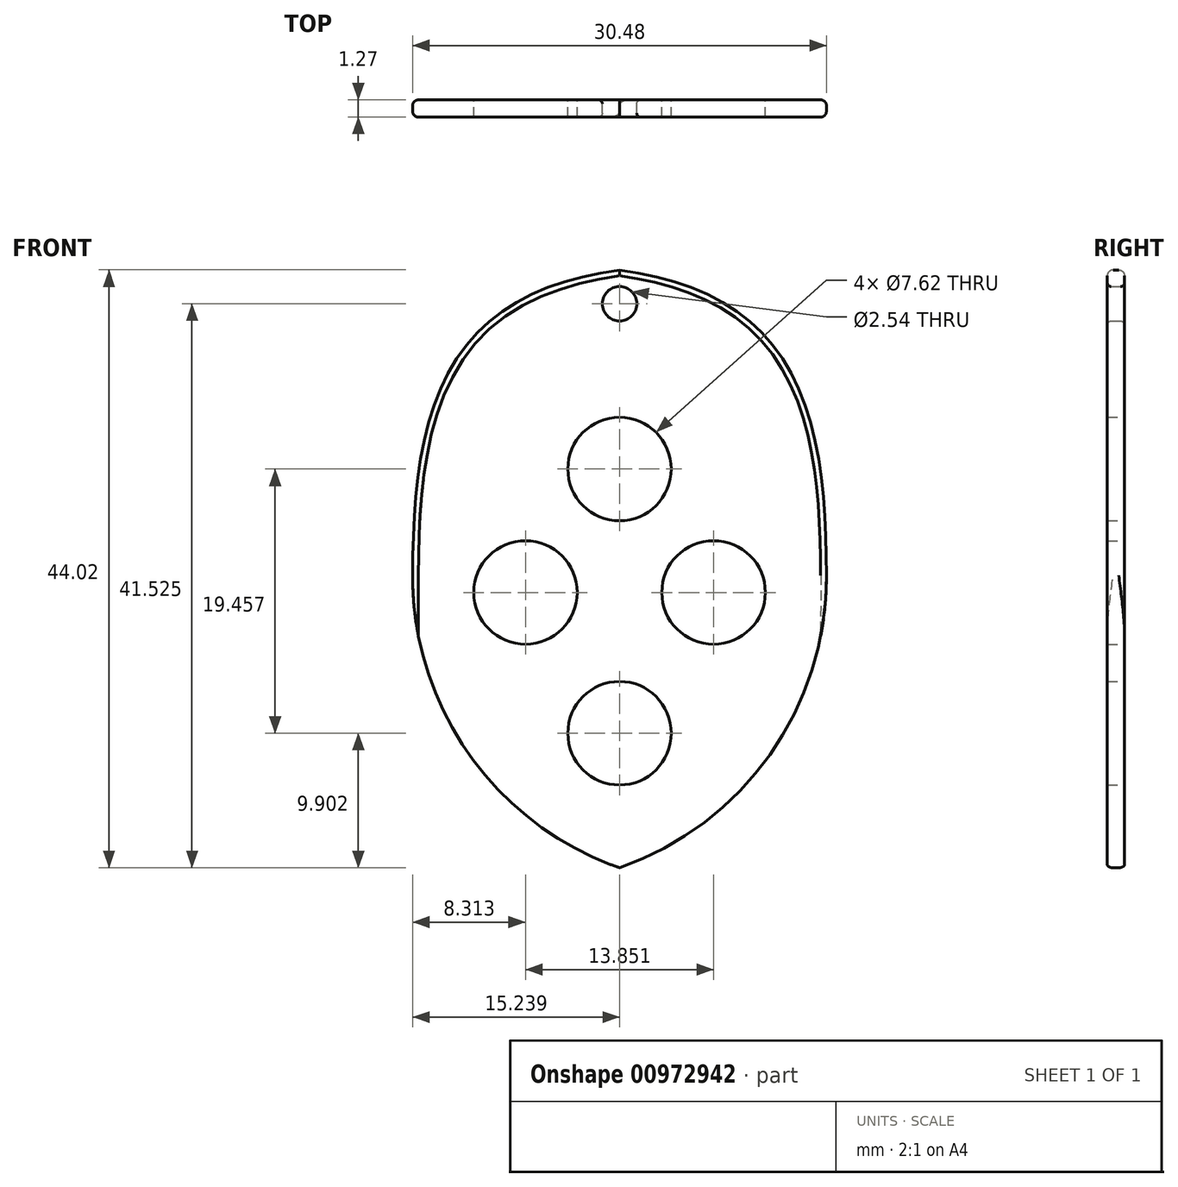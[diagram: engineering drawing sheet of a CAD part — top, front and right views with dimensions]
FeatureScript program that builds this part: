
annotation { "Feature Type Name" : "Feature", "Feature Type Description" : "" }
export const myFeature = defineFeature(function(context is Context, id is Id, definition is map)
    precondition{}
    {
        {
            var Q0;
            Q0=qCreatedBy(makeId("Front.planeOp"),FACE);
            var sketch = newSketch(context, id + "F0", { "sketchPlane" : qUnion([Q0])});
            skLineSegment(sketch, "E0.bottom", {"start": v(-7.7, 19.1) * mm, "end": v(7.55, 19.1) * mm});
            skLineSegment(sketch, "E0.top", {"start": v(-7.7, -26.63) * mm, "end": v(7.55, -26.63) * mm});
            skLineSegment(sketch, "E0.left", {"start": v(-7.7, 19.1) * mm, "end": v(-7.7, -26.63) * mm});
            skLineSegment(sketch, "E0.right", {"start": v(7.55, 19.1) * mm, "end": v(7.55, -26.63) * mm});
            skCircle(sketch, "E1", {"center": v(-7.7, 3.99) * mm, "radius": 3.81 * mm});
            skCircle(sketch, "E2", {"center": v(-7.7, 16.15) * mm, "radius": 1.27 * mm});
            skLineSegment(sketch, "E3", {"start": v(-7.7, 19.1) * mm, "end": v(-22.93, 19.1) * mm});
            skLineSegment(sketch, "E4", {"start": v(-22.93, 19.1) * mm, "end": v(-22.93, -26.63) * mm});
            skLineSegment(sketch, "E5", {"start": v(-22.93, -26.63) * mm, "end": v(-7.7, -26.63) * mm});
            skCircle(sketch, "E6", {"center": v(-7.7, -15.47) * mm, "radius": 3.81 * mm});
            skCircle(sketch, "E7", {"center": v(-14.62, -5.1) * mm, "radius": 3.81 * mm});
            skCircle(sketch, "E8.MirrorC", {"center": v(-0.77, -5.1) * mm, "radius": 3.81 * mm});
            skSolve(sketch);
        }
        {
            var Q0;
            Q0=makeQuery(id+"F0.imprint","IMPRINT",FACE,{"disambiguationData":[TD([[makeQuery(id+"F0.imprint","IMPRINT",EDGE,{"derivedFrom":sQuery(id+"F0.wireOp",EDGE,"E0.bottom")}),-1.0]])]});
            var Q1;
            {var subQ7=sQuery(id+"F0.wireOp",EDGE,"E3");Q1=makeQuery(id+"F0.imprint","IMPRINT",FACE,{"disambiguationData":[TD([[makeQuery(id+"F0.imprint","IMPRINT",EDGE,{"derivedFrom":subQ7}),1.0]])]});}
            extrude(context, id + "F1", {"entities" : qUnion([Q0, Q1]), "depth" : 1.27 * mm, "offsetDistance" : 25.4 * mm});
        }
        {
            var Q0;
            Q0=makeQuery(id+"F1.opExtrude","SWEPT_EDGE",EDGE,{"disambiguationData":[OSD([sQuery(id+"F0.wireOp",EDGE,"E0.bottom"),sQuery(id+"F0.wireOp",EDGE,"E0.right")])]});
            var Q1;
            Q1=makeQuery(id+"F1.opExtrude","SWEPT_EDGE",EDGE,{"disambiguationData":[OSD([sQuery(id+"F0.wireOp",EDGE,"E3"),sQuery(id+"F0.wireOp",EDGE,"E4")])]});
            fillet(context, id + "F2", {"entities" : qUnion([Q0, Q1]), "radius" : 24.53 * mm, "tangentPropagation" : true, "crossSection" : FilletCrossSection.CURVATURE, "magnitude" : 0.6, "defaultsChanged" : false, "vertexSettings" : []});
        }
        {
            var Q0;
            Q0=makeQuery(id+"F1.opExtrude","SWEPT_EDGE",EDGE,{"disambiguationData":[OSD([sQuery(id+"F0.wireOp",EDGE,"E0.top"),sQuery(id+"F0.wireOp",EDGE,"E0.right")])]});
            var Q1;
            Q1=makeQuery(id+"F1.opExtrude","SWEPT_EDGE",EDGE,{"disambiguationData":[OSD([sQuery(id+"F0.wireOp",EDGE,"E4"),sQuery(id+"F0.wireOp",EDGE,"E5")])]});
            fillet(context, id + "F3", {"entities" : qUnion([Q0, Q1]), "radius" : 22.7 * mm, "tangentPropagation" : true, "defaultsChanged" : false, "vertexSettings" : [], "allowEdgeOverflow" : false});
        }
        {
            var Q0;
            {var subQ0=sQuery(id+"F0.wireOp",EDGE,"E0.right");var subQ1=sQuery(id+"F0.wireOp",EDGE,"E0.bottom");Q0=makeQuery(id+"F2.opFillet","BLEND_EDGE",EDGE,{"blendedFrom":[makeQuery(id+"F1.opExtrude","SWEPT_EDGE",EDGE,{"disambiguationData":[OSD([subQ1,subQ0])]}),makeQuery(id+"F1.opExtrude","CAP_FACE",FACE,{"disambiguationData":[OSD([subQ1,sQuery(id+"F0.wireOp",EDGE,"E0.top"),sQuery(id+"F0.wireOp",EDGE,"E0.left"),subQ0,sQuery(id+"F0.wireOp",EDGE,"E1"),sQuery(id+"F0.wireOp",EDGE,"E2")])],"isStart":true})],"blendedInto":[makeQuery(id+"F1.opExtrude","CAP_FACE",FACE,{"disambiguationData":[OSD([subQ1,sQuery(id+"F0.wireOp",EDGE,"E0.top"),sQuery(id+"F0.wireOp",EDGE,"E0.left"),subQ0,sQuery(id+"F0.wireOp",EDGE,"E1"),sQuery(id+"F0.wireOp",EDGE,"E2")])],"isStart":true})]});}
            var Q1;
            {var subQ0=sQuery(id+"F0.wireOp",EDGE,"E0.right");var subQ1=sQuery(id+"F0.wireOp",EDGE,"E0.bottom");Q1=makeQuery(id+"F2.opFillet","BLEND_EDGE",EDGE,{"blendedFrom":[makeQuery(id+"F1.opExtrude","SWEPT_EDGE",EDGE,{"disambiguationData":[OSD([subQ1,subQ0])]}),makeQuery(id+"F1.opExtrude","CAP_FACE",FACE,{"disambiguationData":[OSD([subQ1,sQuery(id+"F0.wireOp",EDGE,"E0.top"),sQuery(id+"F0.wireOp",EDGE,"E0.left"),subQ0,sQuery(id+"F0.wireOp",EDGE,"E1"),sQuery(id+"F0.wireOp",EDGE,"E2")])],"isStart":false})],"blendedInto":[makeQuery(id+"F1.opExtrude","CAP_FACE",FACE,{"disambiguationData":[OSD([subQ1,sQuery(id+"F0.wireOp",EDGE,"E0.top"),sQuery(id+"F0.wireOp",EDGE,"E0.left"),subQ0,sQuery(id+"F0.wireOp",EDGE,"E1"),sQuery(id+"F0.wireOp",EDGE,"E2")])],"isStart":false})]});}
            var Q2;
            {var subQ0=sQuery(id+"F0.wireOp",EDGE,"E4");var subQ1=sQuery(id+"F0.wireOp",EDGE,"E3");Q2=makeQuery(id+"F2.opFillet","BLEND_EDGE",EDGE,{"blendedFrom":[makeQuery(id+"F1.opExtrude","SWEPT_EDGE",EDGE,{"disambiguationData":[OSD([subQ1,subQ0])]}),makeQuery(id+"F1.opExtrude","CAP_FACE",FACE,{"disambiguationData":[OSD([sQuery(id+"F0.wireOp",EDGE,"E0.bottom"),sQuery(id+"F0.wireOp",EDGE,"E0.top"),sQuery(id+"F0.wireOp",EDGE,"E0.right"),sQuery(id+"F0.wireOp",EDGE,"E1"),sQuery(id+"F0.wireOp",EDGE,"E2"),subQ1,subQ0,sQuery(id+"F0.wireOp",EDGE,"E5")])],"isStart":false})],"blendedInto":[makeQuery(id+"F1.opExtrude","CAP_FACE",FACE,{"disambiguationData":[OSD([sQuery(id+"F0.wireOp",EDGE,"E0.bottom"),sQuery(id+"F0.wireOp",EDGE,"E0.top"),sQuery(id+"F0.wireOp",EDGE,"E0.right"),sQuery(id+"F0.wireOp",EDGE,"E1"),sQuery(id+"F0.wireOp",EDGE,"E2"),subQ1,subQ0,sQuery(id+"F0.wireOp",EDGE,"E5")])],"isStart":false})]});}
            var Q3;
            {var subQ0=sQuery(id+"F0.wireOp",EDGE,"E4");var subQ1=sQuery(id+"F0.wireOp",EDGE,"E3");Q3=makeQuery(id+"F2.opFillet","BLEND_EDGE",EDGE,{"blendedFrom":[makeQuery(id+"F1.opExtrude","SWEPT_EDGE",EDGE,{"disambiguationData":[OSD([subQ1,subQ0])]}),makeQuery(id+"F1.opExtrude","CAP_FACE",FACE,{"disambiguationData":[OSD([sQuery(id+"F0.wireOp",EDGE,"E0.bottom"),sQuery(id+"F0.wireOp",EDGE,"E0.top"),sQuery(id+"F0.wireOp",EDGE,"E0.right"),sQuery(id+"F0.wireOp",EDGE,"E1"),sQuery(id+"F0.wireOp",EDGE,"E2"),subQ1,subQ0,sQuery(id+"F0.wireOp",EDGE,"E5")])],"isStart":true})],"blendedInto":[makeQuery(id+"F1.opExtrude","CAP_FACE",FACE,{"disambiguationData":[OSD([sQuery(id+"F0.wireOp",EDGE,"E0.bottom"),sQuery(id+"F0.wireOp",EDGE,"E0.top"),sQuery(id+"F0.wireOp",EDGE,"E0.right"),sQuery(id+"F0.wireOp",EDGE,"E1"),sQuery(id+"F0.wireOp",EDGE,"E2"),subQ1,subQ0,sQuery(id+"F0.wireOp",EDGE,"E5")])],"isStart":true})]});}
            fillet(context, id + "F4", {"entities" : qUnion([Q0, Q1, Q2, Q3]), "radius" : 0.43 * mm, "tangentPropagation" : true, "defaultsChanged" : true, "vertexSettings" : [], "allowEdgeOverflow" : false});
        }
        {
            var Q0;
            Q0=makeQuery(id+"F1.opExtrude","SWEPT_FACE",FACE,{"disambiguationData":[OSD([sQuery(id+"F0.wireOp",EDGE,"E2")])]});
            fillet(context, id + "F5", {"entities" : qUnion([Q0]), "tangentPropagation" : true, "radius" : 0.29 * mm, "defaultsChanged" : true, "vertexSettings" : [], "allowEdgeOverflow" : false});
        }
    });
